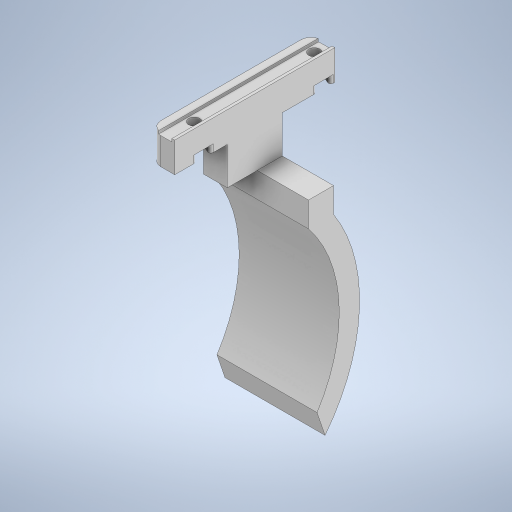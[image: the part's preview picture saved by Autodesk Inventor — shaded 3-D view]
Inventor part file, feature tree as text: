
AUTODESK INVENTOR PART (.ipt)
format: ipt  version: 2024 (Build 280153000, 153)  size: 341,504 bytes
history: native  units: in
note: dims shown in document units (in); Inventor stores cm internally (conversion verified against a paired STEP export)
features: sketch x7, extrude x5, projected_geometry x4, fillet x2, sweep x1
ambient origin geometry x8: Origin, YZ Plane, XZ Plane, XY Plane, X Axis, Y Axis, Z Axis, Center Point
bodies: Solid1 (feature_tree)
feature tree (19):
  extrude  "Extrusion1"  Depth=2.5197in
  extrude  "Extrusion2"  Depth=1.8898in
  extrude  "Extrusion3"  Depth=0.4724in TaperAngle=0.0deg
  fillet  "Fillet1"  Radius=0.0433in
  fillet  "Fillet2"  Radius=0.2126in
  extrude  "Extrusion15"  Depth=0.4724in TaperAngle=0.0deg
  extrude  "Extrusion17"  Depth=0.1181in TaperAngle=0.0deg
  sweep  "Sweep1"
  sketch  "Sketch1"  dims[d1=0.374in d2=2.5197in]
  sketch  "Sketch2"  dims[d3=0.1772in d4=1.8898in]
  sketch  "Sketch3"  dims[d6=0.1457in d7=0.4724in d8=0.0in d9=0.0433in d10=0.2126in]
  projected_geometry  "Projected Loop2"
  projected_geometry  "Projected Loop3"
  projected_geometry  "Projected Loop4"
  projected_geometry  "Projected Loop5"
  sketch  "Sketch15"  dims[d11=0.0472in d12=0.4724in d13=0.0in]
  sketch  "Sketch21"  dims[d14=0.2953in d15=0.1181in d16=0.0in]
  sketch  "Sketch27"  dims[d17=0.1772in d18=0.0394in]
  sketch  "Sketch28"  dims[d19=0.1575in d76=0.4724in d79=0.4331in d80=0.8661in d81=0.5906in d82=0.0in d93=0.3937in d94=0.3937in d95=1.5748in d96=0.3937in d97=0.3937in d98=0.0in d101=2.7559in d102=2.3622in d103=0.0in d104=0.0in d42=0.0197in d43=0.0344in d44=0.0197in d45=0.0344in d46=0.0in d47=0.0in d48=0.0in d49=0.0in d50=0.0in d51=0.0in d52=0.0in d53=0.0in d55=0.0197in d56=0.0344in d57=0.0197in d58=0.0344in d60=0.0197in d61=0.0344in d62=0.0197in d63=0.0344in d72=0.0197in d73=0.0344in d74=0.0197in d75=0.0344in]
